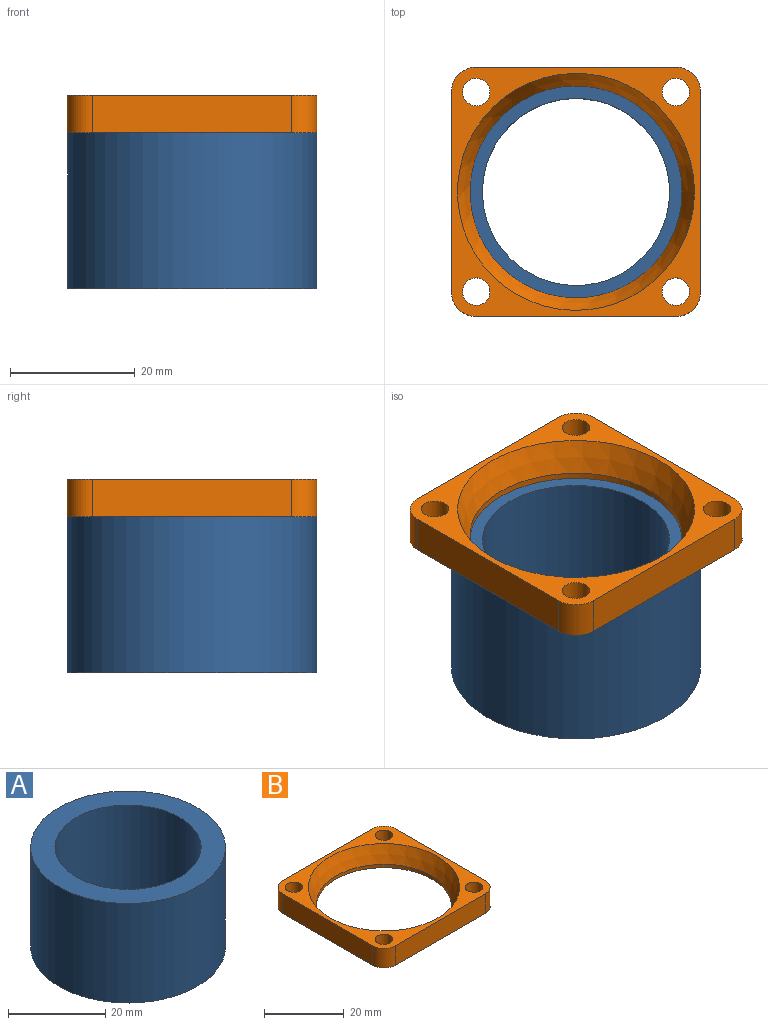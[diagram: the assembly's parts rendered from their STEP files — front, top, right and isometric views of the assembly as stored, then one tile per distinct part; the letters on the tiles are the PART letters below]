
ASSEMBLY  parts=2 mates=1
PART A: 4 faces, bbox 40x40x25 mm
  f0: cylinder r=15mm len=30mm, axis (0,0,-1), area 2356.2mm2, adj f2,f3
  f1: cylinder r=20mm len=40mm, axis (0,0,-1), area 3141.6mm2, adj f2,f3
  f2: plane 40x40mm, normal (0,0,1), area 549.8mm2, adj f0,f1
  f3: plane 40x40mm, normal (0,0,-1), area 549.8mm2, adj f0,f1
PART B: 16 faces, bbox 40x40x6 mm
  f0: plane 32x6mm, normal (1,0,0), area 192mm2, adj f1,f12,f13,f14
  f1: cylinder r=4mm len=6mm, axis (0,0,-1), area 37.7mm2, adj f0,f2,f13,f14
  f2: plane 32x6mm, normal (0,1,0), area 192mm2, adj f1,f3,f13,f14
  f3: cylinder r=4mm len=6mm, axis (0,0,-1), area 37.7mm2, adj f2,f4,f13,f14
  f4: plane 32x6mm, normal (-1,0,0), area 192mm2, adj f3,f5,f13,f14
  f5: cylinder r=4mm len=6mm, axis (0,0,-1), area 37.7mm2, adj f4,f6,f13,f14
  f6: plane 32x6mm, normal (0,-1,0), area 192mm2, adj f5,f12,f13,f14
  f7: cylinder r=2.2mm len=6mm, axis (0,0,-1), area 82.9mm2, adj f13,f14
  f8: cylinder r=2.2mm len=6mm, axis (0,0,-1), area 82.9mm2, adj f13,f14
  f9: cylinder r=2.2mm len=6mm, axis (0,0,-1), area 82.9mm2, adj f13,f14
  f10: cylinder r=17mm len=34mm, axis (0,0,-1), area 106.8mm2, adj f14,f15
  f11: cylinder r=2.2mm len=6mm, axis (0,0,-1), area 82.9mm2, adj f13,f14
  f12: cylinder r=4mm len=6mm, axis (0,0,-1), area 37.7mm2, adj f0,f6,f13,f14
  f13: plane 40x40mm, normal (0,0,1), area 391.3mm2, adj f0,f1,f2,f3,f4,f5,f6,f7
  f14: plane 40x40mm, normal (0,0,-1), area 617.5mm2, adj f0,f1,f2,f3,f4,f5,f6,f7
  f15: cone r=17mm half-angle=21.8deg, axis (0,0,1), area 609mm2, adj f10,f13
PLACE A at identity
PLACE B t=(0,0,25)mm
MATE fastened B.f10 <-> A.f0  axis (0,0,-1) through (0,0,25)mm
